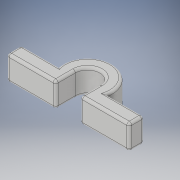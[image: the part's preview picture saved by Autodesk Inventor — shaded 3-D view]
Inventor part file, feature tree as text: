
AUTODESK INVENTOR PART (.ipt)
format: ipt  version: 2019 (Build 230136000, 136)  size: 175,616 bytes
history: native  units: mm
features: extrude x1, fillet x1
ambient origin geometry x8: Origin, YZ Plane, XZ Plane, XY Plane, X Axis, Y Axis, Z Axis, Center Point
bodies: Solid1 (feature_tree)
feature tree (2):
  extrude  "Extrusion1"  Depth=10.0mm TaperAngle=0.0deg
  fillet  "Fillet1"  Radius=0.5mm
